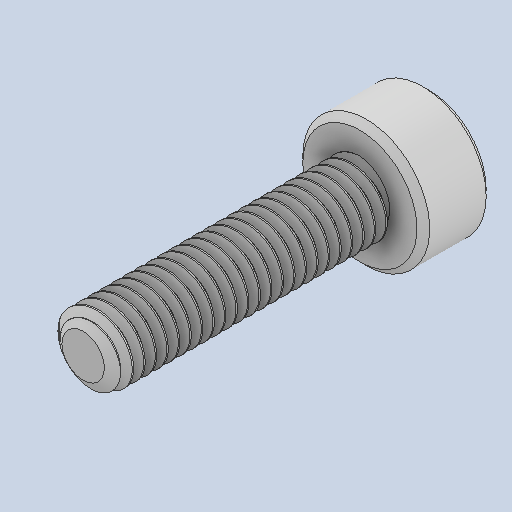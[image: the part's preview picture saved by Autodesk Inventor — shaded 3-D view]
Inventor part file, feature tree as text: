
AUTODESK INVENTOR PART (.ipt)
format: ipt  version: 2023 (Build 270158000, 158)  size: 780,800 bytes
history: native  units: mm
features: chamfer x1
ambient origin geometry x8: Origin, YZ Plane, XZ Plane, XY Plane, X Axis, Y Axis, Z Axis, Center Point
bodies: Solid1 (feature_tree)
feature tree (1):
  chamfer  "Chamfer1"  [1 undecoded]
note: 1 required parameter value undecoded (feature->parameter linkage not recoverable at this tier; creation-order binding heuristic only, values carry confidence <= 0.55)
